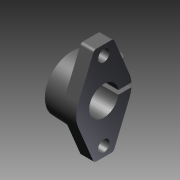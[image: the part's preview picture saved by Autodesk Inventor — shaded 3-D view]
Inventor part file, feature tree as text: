
AUTODESK INVENTOR PART (.ipt)
format: ipt  version: 2011 SP1 (Build 150282100, 282)  size: 216,064 bytes
history: native  units: mm
features: sketch x10, extrude x4, revolve x4, thread x2, hole x2
ambient origin geometry x8: Origin, YZ Plane, XZ Plane, XY Plane, X Axis, Y Axis, Z Axis, Center Point
bodies: Solid1 (feature_tree), body_screw_XY (feature_tree), body_screw_YZ (feature_tree), body_screw_ZX (feature_tree), body_screw_X (feature_tree), body_screw_Y (feature_tree), body_screw_Z (feature_tree), body_screw_Center (feature_tree)
feature tree (22):
  extrude  "Extrusion1"  TaperAngle=360.0deg  [1 undecoded]
  revolve  "Revolution1"  [1 undecoded]
  extrude  "Extrusion2"  TaperAngle=360.0deg  [1 undecoded]
  extrude  "Extrusion3"  Depth=8.884mm TaperAngle=0.0deg
  extrude  "Extrusion4"  Depth=8.884mm TaperAngle=0.0deg
  revolve  "Revolution2"  [1 undecoded]
  revolve  "Revolution3"  [1 undecoded]
  thread  "Thread1"  [1 undecoded]
  revolve  "Revolution4"  [1 undecoded]
  thread  "Thread2"  [1 undecoded]
  hole  "Hole1"  [1 undecoded]
  hole  "Hole2"  [1 undecoded]
  sketch  "Sketch_1"  dims[d0=8.0mm d1=0.0mm d2=360.0deg]
  sketch  "Sketch_2"  dims[d3=22.0mm d4=0.0mm d5=11.0mm d6=0.0mm]
  sketch  "Sketch_3"  dims[d7=20.0mm d8=0.0mm d9=360.0deg]
  sketch  "Sketch_4"  dims[d10=360.0deg d11=8.884mm d12=0.0mm]
  sketch  "Sketch_5"  dims[d13=360.0deg d14=8.884mm d15=0.0mm]
  sketch  "Sketch_6"  dims[d16=7.0mm d17=6.0mm d18=4.0mm d19=2.0mm d20=90.0deg d21=8.0mm d22=0.0mm]
  sketch  "Sketch_7"  dims[d23=7.0mm d24=6.0mm d25=4.0mm d26=2.0mm d27=90.0deg d28=8.0mm d29=0.0mm d30=0.0mm]
  sketch  "Sketch_8"
  sketch  "Sketch9"
  sketch  "Sketch10"
note: 10 required parameter values undecoded (feature->parameter linkage not recoverable at this tier; creation-order binding heuristic only, values carry confidence <= 0.55)